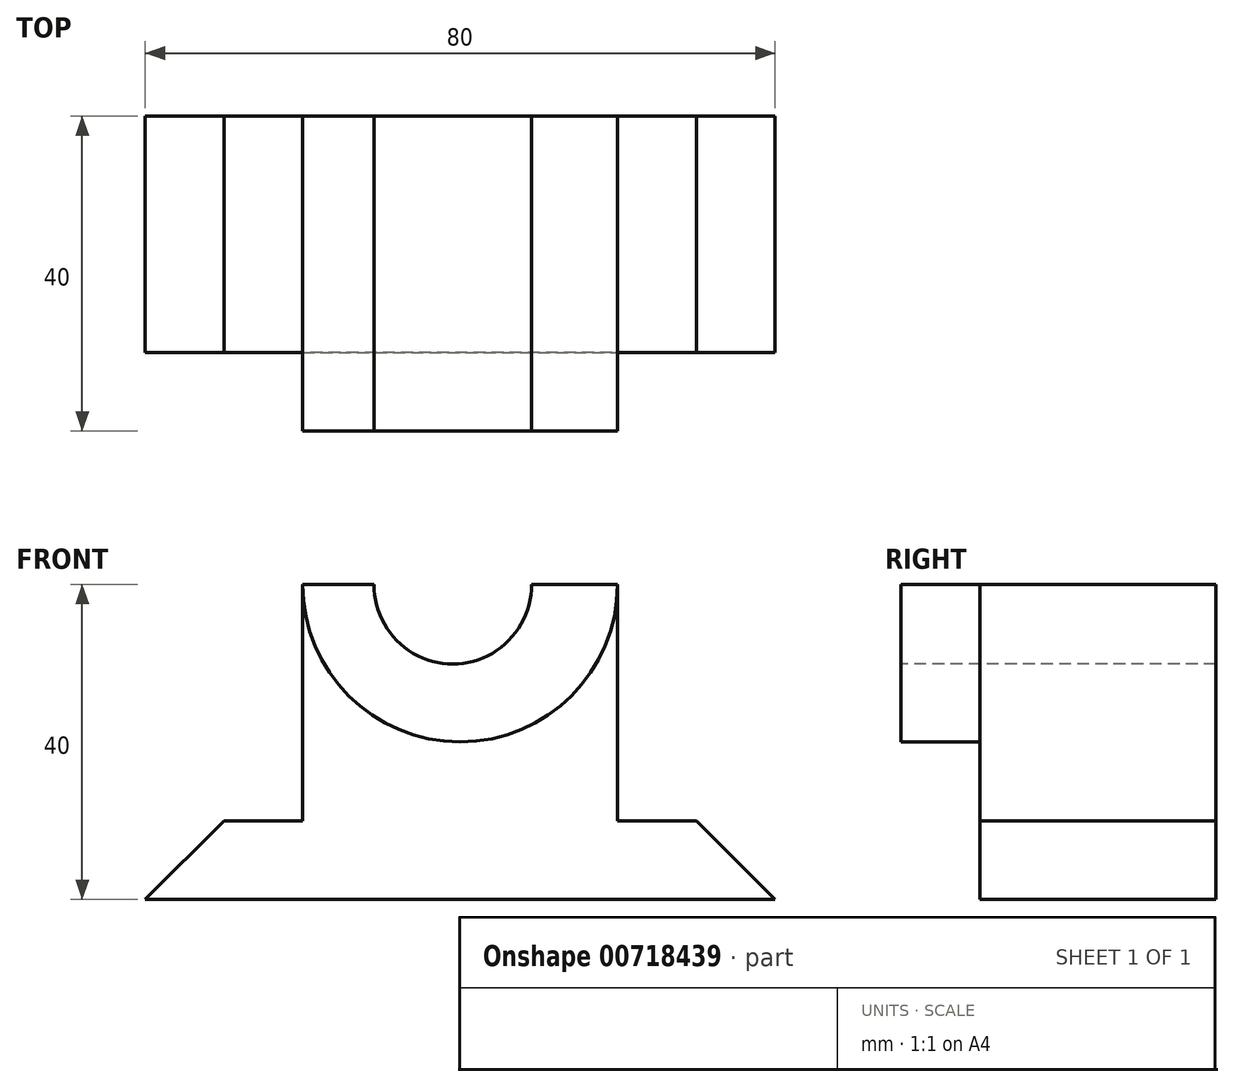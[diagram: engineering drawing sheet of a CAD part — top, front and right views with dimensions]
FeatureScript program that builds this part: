
annotation { "Feature Type Name" : "Feature", "Feature Type Description" : "" }
export const myFeature = defineFeature(function(context is Context, id is Id, definition is map)
    precondition{}
    {
        {
            var Q0;
            Q0=qCreatedBy(makeId("Front.planeOp"),FACE);
            var sketch = newSketch(context, id + "F0", { "sketchPlane" : qUnion([Q0])});
            skLineSegment(sketch, "E0", {"start": v(-1046.95, 0) * mm, "end": v(-1036.95, 10) * mm});
            skLineSegment(sketch, "E1", {"start": v(-1036.95, 10) * mm, "end": v(-976.95, 10) * mm});
            skLineSegment(sketch, "E2", {"start": v(-976.95, 10) * mm, "end": v(-966.95, 0) * mm});
            skLineSegment(sketch, "E3", {"start": v(-966.95, 0) * mm, "end": v(-1046.95, 0) * mm});
            skSolve(sketch);
        }
        {
            var Q0;
            Q0=makeQuery(id+"F0.imprint","IMPRINT",FACE,{"disambiguationData":[TD([[makeQuery(id+"F0.imprint","IMPRINT",EDGE,{"derivedFrom":sQuery(id+"F0.wireOp",EDGE,"E0")}),-1.0]])]});
            extrude(context, id + "F1", {"entities" : qUnion([Q0]), "oppositeDirection" : true, "depth" : 30 * mm, "offsetDistance" : 25.4 * mm});
        }
        {
            var Q0;
            Q0=makeQuery(id+"F1.opExtrude","CAP_FACE",FACE,{"disambiguationData":[OSD([sQuery(id+"F0.wireOp",EDGE,"E0"),sQuery(id+"F0.wireOp",EDGE,"E1"),sQuery(id+"F0.wireOp",EDGE,"E2"),sQuery(id+"F0.wireOp",EDGE,"E3")])],"isStart":true});
            var sketch = newSketch(context, id + "F2", { "sketchPlane" : qUnion([Q0])});
            skLineSegment(sketch, "E4.bottom", {"start": v(-1026.95, 10) * mm, "end": v(-986.95, 10) * mm});
            skLineSegment(sketch, "E4.top", {"start": v(-1026.95, 40) * mm, "end": v(-986.95, 40) * mm});
            skLineSegment(sketch, "E4.left", {"start": v(-1026.95, 10) * mm, "end": v(-1026.95, 40) * mm});
            skLineSegment(sketch, "E4.right", {"start": v(-986.95, 10) * mm, "end": v(-986.95, 40) * mm});
            skSolve(sketch);
        }
        {
            var Q0;
            Q0=makeQuery(id+"F2.imprint","IMPRINT",FACE,{"disambiguationData":[TD([[makeQuery(id+"F2.imprint","IMPRINT",EDGE,{"derivedFrom":sQuery(id+"F2.wireOp",EDGE,"E4.bottom")}),1.0]])]});
            extrude(context, id + "F3", {"entities" : qUnion([Q0]), "operationType" : NewBodyOperationType.ADD, "oppositeDirection" : true, "depth" : 30 * mm, "offsetDistance" : 25 * mm});
        }
        {
            var Q0;
            Q0=makeQuery(id+"F3.boolean.opBoolean","MERGE",FACE,{"derivedFrom":[makeQuery(id+"F1.opExtrude","CAP_FACE",FACE,{"disambiguationData":[OSD([sQuery(id+"F0.wireOp",EDGE,"E0"),sQuery(id+"F0.wireOp",EDGE,"E1"),sQuery(id+"F0.wireOp",EDGE,"E2"),sQuery(id+"F0.wireOp",EDGE,"E3")])],"isStart":true}),makeQuery(id+"F3.opExtrude","CAP_FACE",FACE,{"disambiguationData":[OSD([sQuery(id+"F2.wireOp",EDGE,"E4.bottom"),sQuery(id+"F2.wireOp",EDGE,"E4.top"),sQuery(id+"F2.wireOp",EDGE,"E4.left"),sQuery(id+"F2.wireOp",EDGE,"E4.right")])],"isStart":true})]});
            var sketch = newSketch(context, id + "F4", { "sketchPlane" : qUnion([Q0])});
            skArc(sketch, "E5", {"start": v(-1026.95, 40) * mm, "mid": v(-1006.95, 20) * mm, "end": v(-986.95, 40) * mm});
            skSolve(sketch);
        }
        {
            var Q0;
            Q0 = qSketchRegion(id + "F4", true);
            var Q1;
            Q1=makeQuery(id+"F4.imprint","IMPRINT",FACE,{"disambiguationData":[TD([[makeQuery(id+"F4.imprint","IMPRINT",EDGE,{"derivedFrom":sQuery(id+"F4.wireOp",EDGE,"E5")}),1.0]])]});
            extrude(context, id + "F5", {"entities" : qUnion([Q0, Q1]), "operationType" : NewBodyOperationType.ADD, "depth" : 10 * mm, "offsetDistance" : 25 * mm});
        }
        {
            var Q0;
            Q0=makeQuery(id+"F5.opExtrude","CAP_FACE",FACE,{"disambiguationData":[OSD([sQuery(id+"F2.wireOp",EDGE,"E4.top"),sQuery(id+"F4.wireOp",EDGE,"E5")])],"isStart":false});
            var sketch = newSketch(context, id + "F6", { "sketchPlane" : qUnion([Q0])});
            skArc(sketch, "E6", {"start": v(-1017.89, 40) * mm, "mid": v(-1007.89, 29.91) * mm, "end": v(-997.9, 40) * mm});
            skSolve(sketch);
        }
        {
            var Q0;
            Q0=sQuery(id+"F6.wireOp",VERTEX,"E6.center");
            var Q1;
            Q1=makeQuery(id+"F1.opExtrude","SWEPT_BODY",BODY,{"disambiguationData":[OSD([sQuery(id+"F0.wireOp",EDGE,"E0"),sQuery(id+"F0.wireOp",EDGE,"E1"),sQuery(id+"F0.wireOp",EDGE,"E2"),sQuery(id+"F0.wireOp",EDGE,"E3")])]});
            hole(context, id + "F7", {"style" : HoleStyle.SIMPLE, "endStyle" : HoleEndStyle.THROUGH, "holeDiameter" : 20 * mm, "majorDiameter" : 5 * mm, "isTappedThrough" : true, "tappedDepth" : 12 * mm, "tapClearance" : 3, "locations" : qUnion([Q0]), "scope" : qUnion([Q1])});
        }
    });
